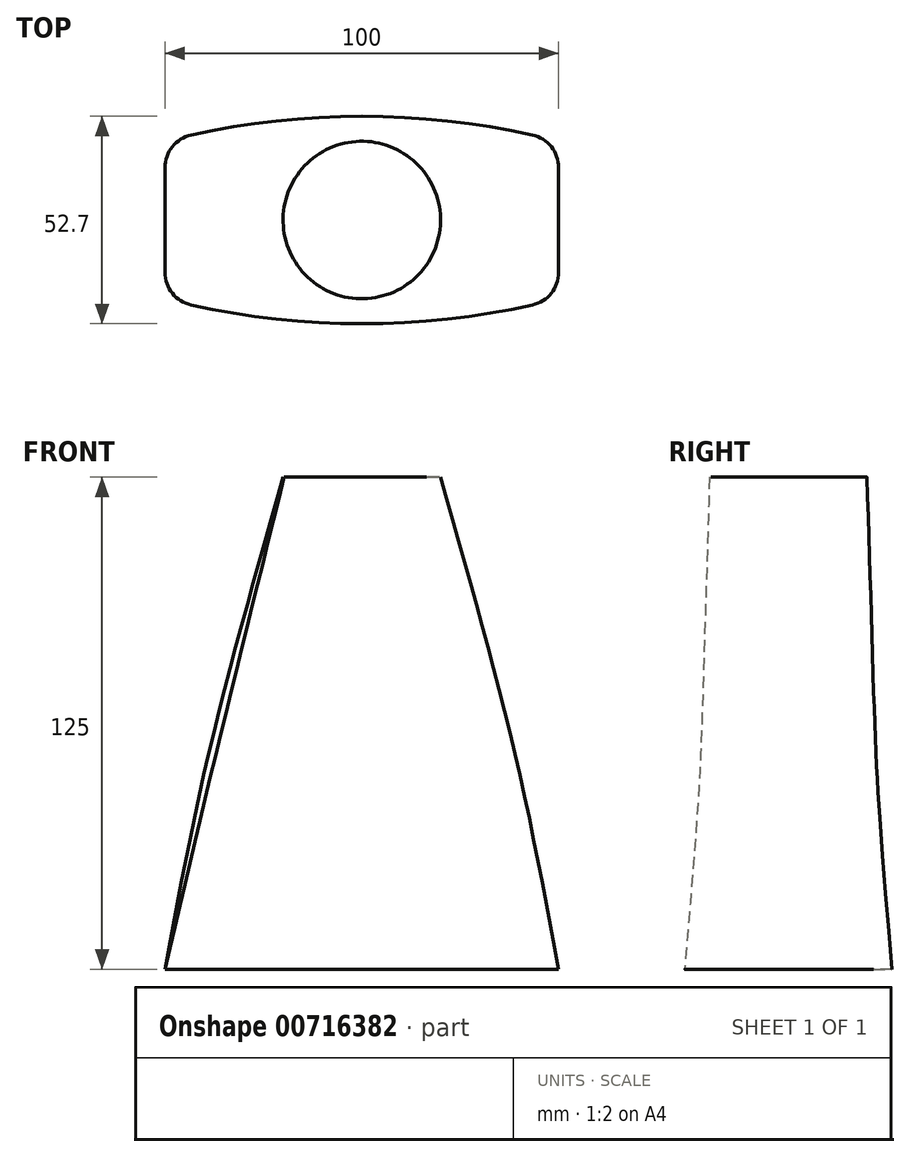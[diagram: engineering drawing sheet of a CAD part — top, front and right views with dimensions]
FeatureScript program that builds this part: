
annotation { "Feature Type Name" : "Feature", "Feature Type Description" : "" }
export const myFeature = defineFeature(function(context is Context, id is Id, definition is map)
    precondition{}
    {
        {
            var Q0;
            Q0=qCreatedBy(makeId("Top.planeOp"),FACE);
            var sketch = newSketch(context, id + "F0", { "sketchPlane" : qUnion([Q0])});
            skLineSegment(sketch, "E0.bottom", {"start": v(-50, -20) * mm, "end": v(50, -20) * mm, "construction": true});
            skLineSegment(sketch, "E0.top", {"start": v(-50, 20) * mm, "end": v(50, 20) * mm, "construction": true});
            skLineSegment(sketch, "E0.left", {"start": v(-50, -13.3) * mm, "end": v(-50, 13.3) * mm});
            skLineSegment(sketch, "E0.right", {"start": v(50, -13.3) * mm, "end": v(50, 13.3) * mm});
            skPoint(sketch, "E0.middle", {"position": v(0, 0) * mm});
            skArc(sketch, "E1", {"start": v(43.34, 21.6) * mm, "mid": v(0, 26.35) * mm, "end": v(-43.34, 21.6) * mm});
            skArc(sketch, "E2", {"start": v(-43.34, -21.6) * mm, "mid": v(0, -26.35) * mm, "end": v(43.34, -21.6) * mm});
            skPoint(sketch, "E3.visualSharp", {"position": v(50, 20) * mm});
            skArc(sketch, "E3.filletArc", {"start": v(50, 13.3) * mm, "mid": v(48.13, 18.62) * mm, "end": v(43.34, 21.6) * mm});
            skPoint(sketch, "E4.visualSharp", {"position": v(50, -20) * mm});
            skArc(sketch, "E4.filletArc", {"start": v(43.34, -21.6) * mm, "mid": v(48.13, -18.62) * mm, "end": v(50, -13.3) * mm});
            skPoint(sketch, "E5.visualSharp", {"position": v(-50, -20) * mm});
            skArc(sketch, "E5.filletArc", {"start": v(-50, -13.3) * mm, "mid": v(-48.13, -18.62) * mm, "end": v(-43.34, -21.6) * mm});
            skPoint(sketch, "E6.visualSharp", {"position": v(-50, 20) * mm});
            skArc(sketch, "E6.filletArc", {"start": v(-43.34, 21.6) * mm, "mid": v(-48.13, 18.62) * mm, "end": v(-50, 13.3) * mm});
            skSolve(sketch);
        }
        {
            var Q0;
            Q0=qCreatedBy(makeId("Top.planeOp"),FACE);
            cPlane(context, id + "F1", {"entities" : qUnion([Q0]), "cplaneType" : CPlaneType.OFFSET, "offset" : 50 * mm, "width" : 150 * mm, "height" : 150 * mm});
        }
        {
            var Q0;
            Q0=qCreatedBy(id+"F1.planeOp",FACE);
            var sketch = newSketch(context, id + "F2", { "sketchPlane" : qUnion([Q0])});
            skEllipse(sketch, "E7", {"center": v(0, 0) * mm, "majorRadius": 40 * mm, "minorRadius": 22.5 * mm, "majorAxis": v(-1, 0)});
            skSolve(sketch);
        }
        {
            var Q0;
            Q0=qCreatedBy(makeId("Top.planeOp"),FACE);
            cPlane(context, id + "F3", {"entities" : qUnion([Q0]), "cplaneType" : CPlaneType.OFFSET, "offset" : 125 * mm, "width" : 150 * mm, "height" : 150 * mm});
        }
        {
            var Q0;
            Q0=qCreatedBy(id+"F3.planeOp",FACE);
            var sketch = newSketch(context, id + "F4", { "sketchPlane" : qUnion([Q0])});
            skCircle(sketch, "E8", {"center": v(0, 0) * mm, "radius": 20 * mm});
            skSolve(sketch);
        }
        {
            var Q0;
            Q0=makeQuery(id+"F0.imprint","IMPRINT",FACE,{"disambiguationData":[TD([[makeQuery(id+"F0.imprint","IMPRINT",EDGE,{"derivedFrom":sQuery(id+"F0.wireOp",EDGE,"E0.left")}),-1.0]])]});
            var Q1;
            Q1=makeQuery(id+"F2.imprint","IMPRINT",FACE,{"disambiguationData":[TD([[makeQuery(id+"F2.imprint","IMPRINT",EDGE,{"derivedFrom":sQuery(id+"F2.wireOp",EDGE,"E7")}),1.0]])]});
            var Q2;
            Q2=makeQuery(id+"F4.imprint","IMPRINT",FACE,{"disambiguationData":[TD([[makeQuery(id+"F4.imprint","IMPRINT",EDGE,{"derivedFrom":sQuery(id+"F4.wireOp",EDGE,"E8")}),1.0]])]});
            loft(context, id + "F5", {"sheetProfilesArray" : [{ "sheetProfileEntities" : qUnion([Q0]) }, { "sheetProfileEntities" : qUnion([Q1]) }, { "sheetProfileEntities" : qUnion([Q2]) }]});
        }
    });
